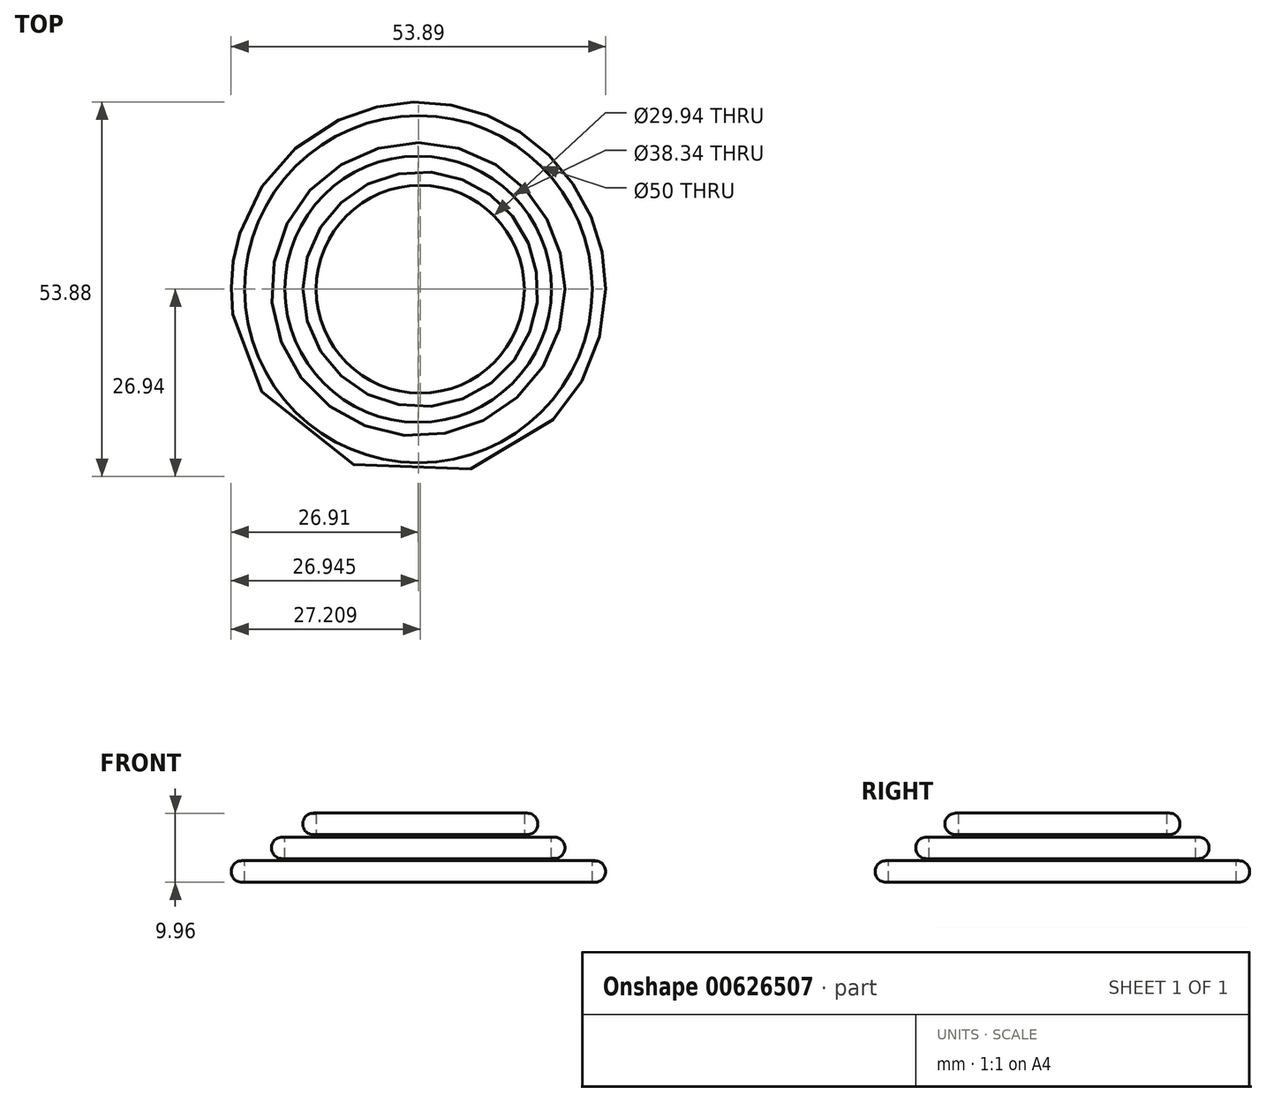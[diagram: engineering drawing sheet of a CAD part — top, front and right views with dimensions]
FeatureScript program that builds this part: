
annotation { "Feature Type Name" : "Feature", "Feature Type Description" : "" }
export const myFeature = defineFeature(function(context is Context, id is Id, definition is map)
    precondition{}
    {
        {
            var Q0;
            Q0=qCreatedBy(makeId("Front.planeOp"),FACE);
            var sketch = newSketch(context, id + "F0", { "sketchPlane" : qUnion([Q0])});
            skLineSegment(sketch, "E0", {"start": v(-5.48, 21.98) * mm, "end": v(-5.48, -16.39) * mm, "construction": true});
            skLineSegment(sketch, "E1", {"start": v(-30.48, 2.5) * mm, "end": v(-30.48, 5.43) * mm});
            skArc(sketch, "E2", {"start": v(-30.52, 5.47) * mm, "mid": v(-32.43, 3.96) * mm, "end": v(-30.52, 2.46) * mm});
            skPoint(sketch, "E3.visualSharp", {"position": v(-30.48, 5.46) * mm});
            skArc(sketch, "E3.filletArc", {"start": v(-30.48, 5.43) * mm, "mid": v(-30.5, 5.46) * mm, "end": v(-30.52, 5.47) * mm});
            skPoint(sketch, "E4.visualSharp", {"position": v(-30.48, 2.46) * mm});
            skArc(sketch, "E4.filletArc", {"start": v(-30.52, 2.46) * mm, "mid": v(-30.5, 2.47) * mm, "end": v(-30.48, 2.5) * mm});
            skSolve(sketch);
        }
        {
            var Q0;
            Q0 = qSketchRegion(id + "F0", true);
            var Q1;
            Q1=sQuery(id+"F0.wireOp",EDGE,"E0");
            revolve(context, id + "F1", {"entities" : qUnion([Q0]), "axis" : qUnion([Q1]), "revolveType" : RevolveType.FULL});
        }
        {
            var Q0;
            Q0=qCreatedBy(makeId("Front.planeOp"),FACE);
            var sketch = newSketch(context, id + "F2", { "sketchPlane" : qUnion([Q0])});
            skLineSegment(sketch, "E5", {"start": v(-6.82, 25.84) * mm, "end": v(-6.82, -12.54) * mm, "construction": true});
            skLineSegment(sketch, "E6", {"start": v(-25.99, 5.9) * mm, "end": v(-25.99, 8.84) * mm});
            skArc(sketch, "E7", {"start": v(-26.02, 8.88) * mm, "mid": v(-27.93, 7.38) * mm, "end": v(-26.02, 5.87) * mm});
            skPoint(sketch, "E8.visualSharp", {"position": v(-25.99, 8.88) * mm});
            skArc(sketch, "E8.filletArc", {"start": v(-25.99, 8.84) * mm, "mid": v(-26, 8.87) * mm, "end": v(-26.02, 8.88) * mm});
            skPoint(sketch, "E9.visualSharp", {"position": v(-25.99, 5.88) * mm});
            skArc(sketch, "E9.filletArc", {"start": v(-26.02, 5.87) * mm, "mid": v(-26, 5.88) * mm, "end": v(-25.99, 5.9) * mm});
            skPoint(sketch, "E10.endSnap0", {"position": v(-25.99, 7.38) * mm});
            skSolve(sketch);
        }
        {
            var Q0;
            Q0 = qSketchRegion(id + "F2", true);
            var Q1;
            Q1=sQuery(id+"F2.wireOp",EDGE,"E5");
            revolve(context, id + "F3", {"entities" : qUnion([Q0]), "axis" : qUnion([Q1]), "revolveType" : RevolveType.FULL});
        }
        {
            var Q0;
            Q0=makeQuery(id+"F3.opRevolve","SWEPT_BODY",BODY,{"disambiguationData":[OSD([sQuery(id+"F2.wireOp",EDGE,"E6"),sQuery(id+"F2.wireOp",EDGE,"E7"),sQuery(id+"F2.wireOp",EDGE,"E8.filletArc"),sQuery(id+"F2.wireOp",EDGE,"E9.filletArc")])]});
            transform(context, id + "F4", {"entities" : qUnion([Q0]), "transformType" : TransformType.TRANSLATION_3D, "dx" : 0.8 * mm, "dy" : 0 * mm, "dz" : 0 * mm, "makeCopy" : false});
        }
        {
            var Q0;
            Q0=makeQuery(id+"F3.opRevolve","SWEPT_BODY",BODY,{"disambiguationData":[OSD([sQuery(id+"F2.wireOp",EDGE,"E6"),sQuery(id+"F2.wireOp",EDGE,"E7"),sQuery(id+"F2.wireOp",EDGE,"E8.filletArc"),sQuery(id+"F2.wireOp",EDGE,"E9.filletArc")])]});
            transform(context, id + "F5", {"entities" : qUnion([Q0]), "transformType" : TransformType.TRANSLATION_3D, "dx" : 1.1 * mm, "dy" : 0 * mm, "dz" : 0 * mm, "makeCopy" : false});
        }
        {
            var Q0;
            Q0=makeQuery(id+"F3.opRevolve","SWEPT_BODY",BODY,{"disambiguationData":[OSD([sQuery(id+"F2.wireOp",EDGE,"E6"),sQuery(id+"F2.wireOp",EDGE,"E7"),sQuery(id+"F2.wireOp",EDGE,"E8.filletArc"),sQuery(id+"F2.wireOp",EDGE,"E9.filletArc")])]});
            transform(context, id + "F6", {"entities" : qUnion([Q0]), "transformType" : TransformType.TRANSLATION_3D, "dx" : -0.6 * mm, "dy" : 0 * mm, "dz" : 0 * mm, "makeCopy" : false});
        }
        {
            var Q0;
            Q0=qCreatedBy(makeId("Front.planeOp"),FACE);
            var sketch = newSketch(context, id + "F7", { "sketchPlane" : qUnion([Q0])});
            skLineSegment(sketch, "E11", {"start": v(-1.05, 32.2) * mm, "end": v(-1.05, -6.17) * mm, "construction": true});
            skLineSegment(sketch, "E12", {"start": v(-20.19, 9.35) * mm, "end": v(-20.19, 12.3) * mm});
            skArc(sketch, "E13", {"start": v(-20.22, 12.33) * mm, "mid": v(-22.13, 10.82) * mm, "end": v(-20.22, 9.32) * mm});
            skPoint(sketch, "E14.visualSharp", {"position": v(-20.19, 12.32) * mm});
            skArc(sketch, "E14.filletArc", {"start": v(-20.19, 12.3) * mm, "mid": v(-20.2, 12.32) * mm, "end": v(-20.22, 12.33) * mm});
            skPoint(sketch, "E15.visualSharp", {"position": v(-20.19, 9.32) * mm});
            skArc(sketch, "E15.filletArc", {"start": v(-20.22, 9.32) * mm, "mid": v(-20.2, 9.33) * mm, "end": v(-20.19, 9.35) * mm});
            skPoint(sketch, "E16.endSnap0", {"position": v(-20.19, 10.82) * mm});
            skLineSegment(sketch, "E17", {"start": v(-5.22, 14.19) * mm, "end": v(-5.22, 20.52) * mm, "construction": true});
            skSolve(sketch);
        }
        {
            var Q0;
            Q0 = qSketchRegion(id + "F7", true);
            var Q1;
            Q1=sQuery(id+"F7.wireOp",EDGE,"E17");
            revolve(context, id + "F8", {"entities" : qUnion([Q0]), "axis" : qUnion([Q1]), "revolveType" : RevolveType.FULL});
        }
    });
